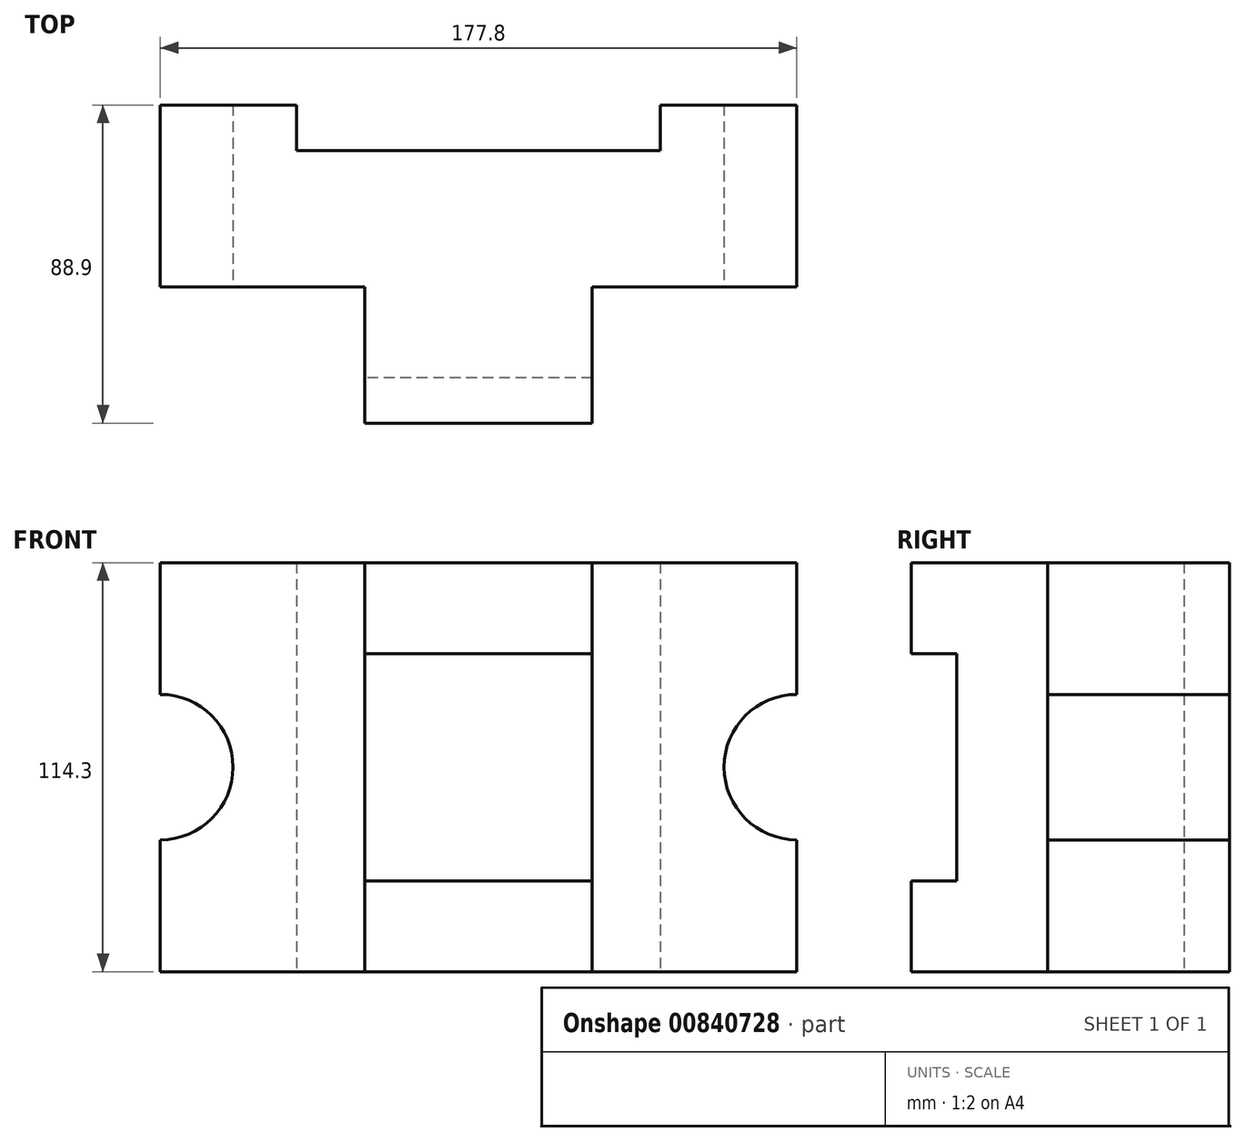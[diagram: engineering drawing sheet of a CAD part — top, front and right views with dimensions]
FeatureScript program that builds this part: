
annotation { "Feature Type Name" : "Feature", "Feature Type Description" : "" }
export const myFeature = defineFeature(function(context is Context, id is Id, definition is map)
    precondition{}
    {
        {
            var Q0;
            Q0=qCreatedBy(makeId("Front.planeOp"),FACE);
            var sketch = newSketch(context, id + "F0", { "sketchPlane" : qUnion([Q0])});
            skLineSegment(sketch, "E0.bottom", {"start": v(-70.24, 62.52) * mm, "end": v(107.56, 62.52) * mm});
            skLineSegment(sketch, "E0.top", {"start": v(-70.24, -51.78) * mm, "end": v(107.56, -51.78) * mm});
            skLineSegment(sketch, "E0.left", {"start": v(-70.24, 62.52) * mm, "end": v(-70.24, 25.7) * mm});
            skLineSegment(sketch, "E0.right", {"start": v(107.56, 62.52) * mm, "end": v(107.56, 25.7) * mm});
            skLineSegment(sketch, "E1", {"start": v(-70.24, -51.78) * mm, "end": v(-70.24, -14.95) * mm});
            skLineSegment(sketch, "E2", {"start": v(-49.92, 5.37) * mm, "end": v(87.24, 5.37) * mm});
            skLineSegment(sketch, "E3", {"start": v(18.66, -51.78) * mm, "end": v(18.66, 62.52) * mm});
            skLineSegment(sketch, "E4", {"start": v(18.66, -51.78) * mm, "end": v(-13.09, -51.78) * mm});
            skLineSegment(sketch, "E5", {"start": v(-13.09, -51.78) * mm, "end": v(18.66, -51.78) * mm});
            skLineSegment(sketch, "E6", {"start": v(-13.09, -51.78) * mm, "end": v(-13.09, 62.52) * mm});
            skLineSegment(sketch, "E7", {"start": v(-13.09, 62.52) * mm, "end": v(50.41, 62.52) * mm});
            skLineSegment(sketch, "E8", {"start": v(50.41, 62.52) * mm, "end": v(50.41, -51.78) * mm});
            skArc(sketch, "E9", {"start": v(-70.24, -14.95) * mm, "mid": v(-49.92, 5.37) * mm, "end": v(-70.24, 25.7) * mm});
            skArc(sketch, "E10.MirrorC", {"start": v(107.56, -14.95) * mm, "mid": v(87.24, 5.37) * mm, "end": v(107.56, 25.7) * mm});
            skLineSegment(sketch, "E11.trimOffspring", {"start": v(-70.24, -14.95) * mm, "end": v(-70.24, -51.78) * mm});
            skLineSegment(sketch, "E12.trimOffspring", {"start": v(107.56, -14.95) * mm, "end": v(107.56, -51.78) * mm});
            skSolve(sketch);
        }
        {
            var Q0;
            {var subQ7=sQuery(id+"F0.wireOp",EDGE,"E0.left");Q0=makeQuery(id+"F0.imprint","IMPRINT",FACE,{"disambiguationData":[TD([[makeQuery(id+"F0.imprint","IMPRINT",EDGE,{"derivedFrom":subQ7}),1.0]])]});}
            var Q1;
            {var subQ7=sQuery(id+"F0.wireOp",EDGE,"E1");Q1=makeQuery(id+"F0.imprint","IMPRINT",FACE,{"disambiguationData":[TD([[makeQuery(id+"F0.imprint","IMPRINT",EDGE,{"derivedFrom":subQ7}),-1.0]])]});}
            var Q2;
            {var subQ0=sQuery(id+"F0.wireOp",EDGE,"E12.trimOffspring");Q2=makeQuery(id+"F0.imprint","IMPRINT",FACE,{"disambiguationData":[TD([[makeQuery(id+"F0.imprint","IMPRINT",EDGE,{"derivedFrom":subQ0}),-1.0]])]});}
            var Q3;
            {var subQ7=sQuery(id+"F0.wireOp",EDGE,"E0.right");Q3=makeQuery(id+"F0.imprint","IMPRINT",FACE,{"disambiguationData":[TD([[makeQuery(id+"F0.imprint","IMPRINT",EDGE,{"derivedFrom":subQ7}),-1.0]])]});}
            var Q4;
            {var subQ0=sQuery(id+"F0.wireOp",EDGE,"E6");var subQ1=sQuery(id+"F0.wireOp",EDGE,"E0.bottom");var subQ2=makeQuery(id+"F0.imprint","INTERSECT",VERTEX,{"derivedFrom":[subQ1,subQ0]});Q4=makeQuery(id+"F0.imprint","IMPRINT",FACE,{"disambiguationData":[TD([[makeQuery(id+"F0.imprint","IMPRINT",EDGE,{"disambiguationData":[TD([[subQ2,-1.0]])],"derivedFrom":subQ1}),-1.0]])]});}
            var Q5;
            {var subQ0=sQuery(id+"F0.wireOp",EDGE,"E3");var subQ1=sQuery(id+"F0.wireOp",EDGE,"E0.top");var subQ2=makeQuery(id+"F0.imprint","INTERSECT",VERTEX,{"derivedFrom":[subQ1,subQ0]});Q5=makeQuery(id+"F0.imprint","IMPRINT",FACE,{"disambiguationData":[TD([[makeQuery(id+"F0.imprint","IMPRINT",EDGE,{"disambiguationData":[TD([[subQ2,1.0]])],"derivedFrom":subQ1}),1.0]])]});}
            var Q6;
            {var subQ0=sQuery(id+"F0.wireOp",EDGE,"E8");var subQ1=sQuery(id+"F0.wireOp",EDGE,"E0.top");var subQ2=makeQuery(id+"F0.imprint","INTERSECT",VERTEX,{"derivedFrom":[subQ1,subQ0]});Q6=makeQuery(id+"F0.imprint","IMPRINT",FACE,{"disambiguationData":[TD([[makeQuery(id+"F0.imprint","IMPRINT",EDGE,{"disambiguationData":[TD([[subQ2,1.0]])],"derivedFrom":subQ1}),1.0]])]});}
            var Q7;
            {var subQ0=sQuery(id+"F0.wireOp",EDGE,"E8");var subQ1=sQuery(id+"F0.wireOp",EDGE,"E0.bottom");var subQ2=makeQuery(id+"F0.imprint","INTERSECT",VERTEX,{"derivedFrom":[subQ1,subQ0]});Q7=makeQuery(id+"F0.imprint","IMPRINT",FACE,{"disambiguationData":[TD([[makeQuery(id+"F0.imprint","IMPRINT",EDGE,{"disambiguationData":[TD([[subQ2,1.0]])],"derivedFrom":subQ1}),-1.0]])]});}
            extrude(context, id + "F1", {"entities" : qUnion([Q0, Q1, Q2, Q3, Q4, Q5, Q6, Q7]), "oppositeDirection" : true, "depth" : 50.8 * mm, "offsetDistance" : 25.4 * mm});
        }
        {
            var Q0;
            Q0=makeQuery(id+"F1.opExtrude","CAP_FACE",FACE,{"disambiguationData":[OSD([sQuery(id+"F0.wireOp",EDGE,"E0.bottom"),sQuery(id+"F0.wireOp",EDGE,"E0.top"),sQuery(id+"F0.wireOp",EDGE,"E0.left"),sQuery(id+"F0.wireOp",EDGE,"E0.right"),sQuery(id+"F0.wireOp",EDGE,"E1"),sQuery(id+"F0.wireOp",EDGE,"E9"),sQuery(id+"F0.wireOp",EDGE,"E10.MirrorC"),sQuery(id+"F0.wireOp",EDGE,"E12.trimOffspring")])],"isStart":true});
            var sketch = newSketch(context, id + "F2", { "sketchPlane" : qUnion([Q0])});
            skLineSegment(sketch, "E13", {"start": v(-70.24, -51.78) * mm, "end": v(107.56, -51.78) * mm});
            skLineSegment(sketch, "E14", {"start": v(-70.24, -51.78) * mm, "end": v(18.66, -51.78) * mm});
            skLineSegment(sketch, "E15", {"start": v(18.66, -51.78) * mm, "end": v(18.66, 62.52) * mm});
            skLineSegment(sketch, "E16", {"start": v(18.66, 62.52) * mm, "end": v(50.41, 62.52) * mm});
            skLineSegment(sketch, "E17", {"start": v(50.41, 62.52) * mm, "end": v(50.41, -51.78) * mm});
            skLineSegment(sketch, "E18", {"start": v(50.41, -51.78) * mm, "end": v(-13.09, -51.78) * mm});
            skLineSegment(sketch, "E19", {"start": v(-13.09, -51.78) * mm, "end": v(-13.09, 62.52) * mm});
            skLineSegment(sketch, "E20", {"start": v(-13.09, 62.52) * mm, "end": v(18.66, 62.52) * mm});
            skLineSegment(sketch, "E21", {"start": v(50.41, 62.52) * mm, "end": v(50.41, 37.12) * mm});
            skLineSegment(sketch, "E22", {"start": v(50.41, 37.12) * mm, "end": v(-13.09, 37.12) * mm});
            skLineSegment(sketch, "E23", {"start": v(50.41, -51.78) * mm, "end": v(50.41, -26.38) * mm});
            skLineSegment(sketch, "E24", {"start": v(50.41, -26.38) * mm, "end": v(-13.09, -26.38) * mm});
            skLineSegment(sketch, "E25", {"start": v(50.41, -26.38) * mm, "end": v(50.41, -51.78) * mm});
            skSolve(sketch);
        }
        {
            var Q0;
            {var subQ0=sQuery(id+"F2.wireOp",EDGE,"E16");Q0=makeQuery(id+"F2.imprint","IMPRINT",FACE,{"disambiguationData":[TD([[makeQuery(id+"F2.imprint","IMPRINT",EDGE,{"derivedFrom":subQ0}),-1.0]])]});}
            var Q1;
            {var subQ0=sQuery(id+"F2.wireOp",EDGE,"E20");Q1=makeQuery(id+"F2.imprint","IMPRINT",FACE,{"disambiguationData":[TD([[makeQuery(id+"F2.imprint","IMPRINT",EDGE,{"derivedFrom":subQ0}),-1.0]])]});}
            var Q2;
            {var subQ0=sQuery(id+"F2.wireOp",EDGE,"E18");var subQ1=sQuery(id+"F2.wireOp",EDGE,"E15");var subQ2=makeQuery(id+"F2.imprint","INTERSECT",VERTEX,{"derivedFrom":[subQ1,subQ0]});Q2=makeQuery(id+"F2.imprint","IMPRINT",FACE,{"disambiguationData":[TD([[makeQuery(id+"F2.imprint","IMPRINT",EDGE,{"disambiguationData":[TD([[subQ2,-1.0]])],"derivedFrom":subQ1}),1.0]])]});}
            var Q3;
            {var subQ5=sQuery(id+"F2.wireOp",EDGE,"E25");Q3=makeQuery(id+"F2.imprint","IMPRINT",FACE,{"disambiguationData":[TD([[makeQuery(id+"F2.imprint","IMPRINT",EDGE,{"derivedFrom":subQ5}),-1.0]])]});}
            var Q4;
            {var subQ5=sQuery(id+"F2.wireOp",EDGE,"E17");Q4=makeQuery(id+"F2.imprint","IMPRINT",FACE,{"disambiguationData":[TD([[makeQuery(id+"F2.imprint","IMPRINT",EDGE,{"derivedFrom":subQ5}),-1.0]])]});}
            var Q5;
            {var subQ0=sQuery(id+"F2.wireOp",EDGE,"E24");var subQ1=sQuery(id+"F2.wireOp",EDGE,"E15");var subQ2=makeQuery(id+"F2.imprint","INTERSECT",VERTEX,{"derivedFrom":[subQ1,subQ0]});Q5=makeQuery(id+"F2.imprint","IMPRINT",FACE,{"disambiguationData":[TD([[makeQuery(id+"F2.imprint","IMPRINT",EDGE,{"disambiguationData":[TD([[subQ2,-1.0]])],"derivedFrom":subQ1}),1.0]])]});}
            extrude(context, id + "F3", {"entities" : qUnion([Q0, Q1, Q2, Q3, Q4, Q5]), "operationType" : NewBodyOperationType.ADD, "depth" : 38.1 * mm, "offsetDistance" : 25.4 * mm});
        }
        {
            var Q0;
            Q0=makeQuery(id+"F3.opExtrude","CAP_FACE",FACE,{"disambiguationData":[OSD([sQuery(id+"F2.wireOp",EDGE,"E16"),sQuery(id+"F2.wireOp",EDGE,"E17"),sQuery(id+"F2.wireOp",EDGE,"E18"),sQuery(id+"F2.wireOp",EDGE,"E19"),sQuery(id+"F2.wireOp",EDGE,"E20"),sQuery(id+"F2.wireOp",EDGE,"E21"),sQuery(id+"F2.wireOp",EDGE,"E25")])],"isStart":false});
            var sketch = newSketch(context, id + "F4", { "sketchPlane" : qUnion([Q0])});
            skLineSegment(sketch, "E26", {"start": v(50.41, 62.52) * mm, "end": v(50.41, 37.12) * mm});
            skLineSegment(sketch, "E27", {"start": v(50.41, 37.12) * mm, "end": v(-13.09, 37.12) * mm});
            skLineSegment(sketch, "E28", {"start": v(50.41, -51.78) * mm, "end": v(50.41, -26.38) * mm});
            skLineSegment(sketch, "E29", {"start": v(50.41, -26.38) * mm, "end": v(-13.09, -26.38) * mm});
            skSolve(sketch);
        }
        {
            var Q0;
            {var subQ0=sQuery(id+"F4.wireOp",EDGE,"E27");Q0=makeQuery(id+"F4.imprint","IMPRINT",FACE,{"disambiguationData":[TD([[makeQuery(id+"F4.imprint","IMPRINT",EDGE,{"derivedFrom":subQ0}),1.0]])]});}
            extrude(context, id + "F5", {"entities" : qUnion([Q0]), "operationType" : NewBodyOperationType.REMOVE, "oppositeDirection" : true, "depth" : 12.7 * mm, "offsetDistance" : 25.4 * mm});
        }
        {
            var Q0;
            Q0=makeQuery(id+"F1.opExtrude","CAP_FACE",FACE,{"disambiguationData":[OSD([sQuery(id+"F0.wireOp",EDGE,"E0.bottom"),sQuery(id+"F0.wireOp",EDGE,"E0.top"),sQuery(id+"F0.wireOp",EDGE,"E0.left"),sQuery(id+"F0.wireOp",EDGE,"E0.right"),sQuery(id+"F0.wireOp",EDGE,"E1"),sQuery(id+"F0.wireOp",EDGE,"E9"),sQuery(id+"F0.wireOp",EDGE,"E10.MirrorC"),sQuery(id+"F0.wireOp",EDGE,"E12.trimOffspring")])],"isStart":false});
            var sketch = newSketch(context, id + "F6", { "sketchPlane" : qUnion([Q0])});
            skLineSegment(sketch, "E30", {"start": v(-18.66, 62.52) * mm, "end": v(32.14, 62.52) * mm});
            skLineSegment(sketch, "E31.bottom", {"start": v(32.14, 62.52) * mm, "end": v(-69.65, 62.52) * mm});
            skLineSegment(sketch, "E32.bottom", {"start": v(-51.74, -51.78) * mm, "end": v(-54.45, -51.78) * mm});
            skLineSegment(sketch, "E33.bottom", {"start": v(32.14, 62.52) * mm, "end": v(-69.46, 62.52) * mm});
            skLineSegment(sketch, "E33.top", {"start": v(32.14, -51.78) * mm, "end": v(-69.46, -51.78) * mm});
            skLineSegment(sketch, "E33.left", {"start": v(32.14, 62.52) * mm, "end": v(32.14, -51.78) * mm});
            skLineSegment(sketch, "E33.right", {"start": v(-69.46, 62.52) * mm, "end": v(-69.46, -51.78) * mm});
            skSolve(sketch);
        }
        {
            var Q0;
            {var subQ2=sQuery(id+"F6.wireOp",EDGE,"E33.left");Q0=makeQuery(id+"F6.imprint","IMPRINT",FACE,{"disambiguationData":[TD([[makeQuery(id+"F6.imprint","IMPRINT",EDGE,{"derivedFrom":subQ2}),-1.0]])]});}
            extrude(context, id + "F7", {"entities" : qUnion([Q0]), "operationType" : NewBodyOperationType.REMOVE, "oppositeDirection" : true, "depth" : 12.7 * mm, "offsetDistance" : 25.4 * mm});
        }
    });
